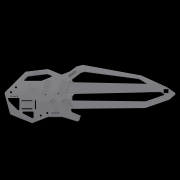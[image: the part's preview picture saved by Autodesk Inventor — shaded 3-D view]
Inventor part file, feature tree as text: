
AUTODESK INVENTOR PART (.ipt)
format: ipt  version: 2020 (Build 240168000, 168)  size: 9,547,776 bytes
history: native  units: in
note: dims shown in document units (in); Inventor stores cm internally (conversion verified against a paired STEP export)
features: other x165, extrude x70, fillet x51, projected_geometry x6, sketch x5, hole x4, loft x3, reference x2, plane x1, move_body x1
ambient origin geometry x8: Origin, YZ Plane, XZ Plane, XY Plane, X Axis, Y Axis, Z Axis, Center Point
bodies: Body (feature_tree), BodyFeature (feature_tree), BodyCut (feature_tree), BodyCutFeature (feature_tree), BodyCutFilletFeature (feature_tree), BodyCutCombineFeature (feature_tree), BodyCutEdgeFilletFeature (feature_tree), BodyRibFrontFilletsFeature (feature_tree), BodyBackRibFilletsFeature (feature_tree), BodyFretboardFilletsFeature (feature_tree), BodyFrontTopFilletsFeature (feature_tree), BodyFrontBottomFilletsFeature (feature_tree), BodyFrontNeckFilletsFeature (feature_tree), Solid22 (feature_tree), Solid23 (feature_tree), Solid62 (feature_tree), Solid64 (feature_tree), Solid65 (feature_tree), Solid68 (feature_tree), Solid50 (feature_tree), Solid52 (feature_tree), Solid54 (feature_tree), Solid56 (feature_tree), Solid57 (feature_tree), Solid59 (feature_tree)
feature tree (308):
  other  "MainBody"
  extrude  "NeckMountsProfileFeature"  Depth=0.5in TaperAngle=0.0deg
  other  "NeckPlane"
  extrude  "8StringFeature"  Depth=4.5in
  extrude  "6StringFeature"  Depth=1.12in
  extrude  "HornFeature"  Depth=0.6788in
  other  "6StringNeckFeature"
  other  "8StringNeckFeature"
  fillet  "InsideCornerFilletsFeature1/8"  Radius=0.6788in
  fillet  "OutsideFilletsFeature1/2"  Radius=0.125in
  fillet  "NeckMountOutsideFilletsFeature1/4"  Radius=0.5in
  fillet  "TipFilletsFeature1/8"  Radius=0.125in
  fillet  "BottomHornTipFilletFeature1/10"  Radius=0.1in
  fillet  "BottomHornFilletsFeature1/8"  Radius=0.125in
  fillet  "InsideHandleFilletsFeature1/2"  Radius=0.5in
  fillet  "InsideHandleFilletsFeature1/8"  Radius=0.125in
  fillet  "InsideTopHornFilletsFeature1/4"  Radius=0.25in
  fillet  "InsideTopHornFilletsFeature1/2"  Radius=0.5in
  fillet  "InsideBottomHornFilletsFeature1/4"  Radius=0.25in
  other  "PickupsOriginal"
  other  "MiddlePlane"
  other  "PickupsCustom"
  other  "PickupsModified"
  extrude  "TopPickupsIndentFeature"  Depth=0.05in
  extrude  "BottomPickupsIndentFeature"  Depth=0.05in
  extrude  "TopPickupHolesFeature"  Depth=0.05in
  extrude  "BottomPickupHolesFeature"  Depth=0.05in
  fillet  "PickupIndentFilletsFeature"  Radius=1.1649in
  other  "Frets"
  other  "FretsPreview"
  other  "TopHornHandleIndent"
  extrude  "TopHornBodyHandleFeature"  Depth=0.05in
  extrude  "TopHornHornHandleFeature"  Depth=0.05in
  other  "HornSculptFeature"
  other  "TopHornHandleFront"
  extrude  "TopHornHandleFrontFeature"  Depth=0.05in
  extrude  "TopHornHandleFront2Feature"  Depth=0.05in
  extrude  "TopHornHandleFront3Feature"  TaperAngle=45.0deg  [1 undecoded]
  other  "TopHornHandleBack"
  extrude  "TopHornHandleBackFeature"  TaperAngle=120.0deg  [1 undecoded]
  extrude  "TopHornHandleBack2Feature"  Depth=0.05in
  extrude  "TopHandleFeature"  Depth=0.05in
  extrude  "TopHandleFrontFeature"  Depth=0.05in
  extrude  "TopHandleBackFeature"  Depth=0.05in
  other  "Tuners"
  hole  "TunerHolesFeature"  [1 undecoded]
  other  "LogoMount"
  extrude  "LogoMountFeature"  Depth=0.05in
  other  "SideProfile"
  extrude  "SideProfileFeature"  Depth=0.05in
  other  "KeyboardCompartmentSidePlane"
  extrude  "KeyboardCompartmentFeature"  Depth=0.05in
  fillet  "KeyboardCompartmentFilletsFeature"  Radius=0.101in
  other  "ControlsBottom"
  other  "ControlsTop2"
  other  "ControlsTop1"
  extrude  "ControlsTop1Feature"  Depth=0.05in
  extrude  "ControlsTop2Feature"  Depth=0.05in
  extrude  "ControlsBottomFeature"  Depth=0.05in
  other  "HornSculptSideProfileFeature"
  fillet  "HornFretboardFilletFeature"  Radius=0.933in
  other  "ElectronicsCompartments"
  other  "InsideFacePlane1"
  other  "InsideFacePlane2"
  other  "InsideFacePlane3"
  extrude  "ElectronicCompartmentTopFeature"  Depth=0.05in
  extrude  "ElectronicCompartmentBottomFeature"  Depth=0.05in
  other  "ElectronicCompartmentsSculpt1Feature"
  other  "ElectronicCompartmentsSculpt2Feature"
  other  "ElectronicCompartmentsSculpt3Feature"
  other  "ElectronicCompartmentsSubtractFeature"
  extrude  "ElectronicCompartmentsSubtract2Feature"  Depth=0.05in
  fillet  "ElectronicCompartmentFillets1Feature"  Radius=3.5in
  fillet  "ElectronicCompartmentFillets2Feature"  Radius=1.277in
  extrude  "ControlIndentsBottomFeature"  Depth=0.05in
  fillet  "ElectronicCompartmentFillets3Feature"  Radius=1.5in
  fillet  "ElectronicCompartmentFillets4Feature"  Radius=1.0857in
  extrude  "ControlIndentsTopFeature"  Depth=0.05in
  other  "ControlIndents2Top"
  extrude  "ControlIndents2TopFeature"  Depth=0.05in
  fillet  "ControlIndents3FilletsFeature"  Radius=4.5in
  extrude  "ControlIndents2RecutFeature"  Depth=0.05in
  fillet  "ElectronicCompartmentInsideFilletsFeature"  Radius=0.1512in
  other  "BottomBridgePickupWirePlane"
  extrude  "BottomBridgePickupWireHoleFeature"  Depth=0.05in
  other  "BottomNeckPickupWirePlane"
  extrude  "BottomNeckPickupWireFeature"  Depth=0.05in
  extrude  "TopPickupWireFeature"  Depth=0.05in
  other  "SeaboardBlockCircuitboardMounts"
  extrude  "SeaboardBlockMountStemFeature"  Depth=0.05in
  extrude  "SeaboardBlockMountsFeature"  Depth=0.05in
  other  "SeaboardBlockKeyMounts"
  extrude  "SeaboardBlockKeyMountsFeature"  Depth=0.05in
  extrude  "SeaboardBlockRibbonsFeature"  Depth=0.05in
  extrude  "TunersTopFeature"  Depth=0.05in
  extrude  "TunersMiddleFeature"  Depth=0.05in
  extrude  "TunersBottomFeature"  Depth=0.05in
  fillet  "TunerFilletsFeature"  Radius=1.1386in
  extrude  "NeckCutFeature"  Depth=0.05in
  fillet  "NeckCutFilletFeature"  Radius=4.009in
  other  "NeckCutCombineFeature"
  fillet  "NeckCutEdgeFilletFeature"  Radius=1.481in
  fillet  "NeckCutCornerFilletsFeature"  Radius=0.25in
  extrude  "NeckMountsFeature"  Depth=0.05in
  extrude  "FretMarkersTopFeature"  Depth=0.05in
  extrude  "FretMarkersBottomFeature"  Depth=0.05in
  extrude  "FretsPreviewFeature"  TaperAngle=0.0deg  [1 undecoded]
  extrude  "FretLocksPreviewFeature"  Depth=0.3937in
  hole  "FretLocksHolesFeature"  [1 undecoded]
  extrude  "TopHornHandleBodyFeature"  Depth=0.05in
  other  "TopHornSculpt3Feature"
  other  "TopHornSculpt4Feature"
  other  "TopHornSculpt5Feature"
  fillet  "TopHornHandleBodyFilletsFeature"  Radius=0.9256in
  fillet  "TopHornHandleFilletsFeature"  [1 undecoded]
  other  "TopHornAdjustFeature"
  fillet  "TopHornAdjustFilletFeature"  [1 undecoded]
  other  "HandlePlane1"
  other  "HandlePlane2"
  other  "Handle"
  extrude  "HandleBackFeature"  Depth=0.05in
  extrude  "HandleFrontFeature"  Depth=0.05in
  other  "HandleSculpt1Feature"
  other  "HandleSculpt2Feature"
  other  "HandleSculpt3Feature"
  other  "HandleSculpt4Feature"
  other  "HandleSculpt5Feature"
  other  "HandleSculpt6Feature"
  other  "HandleEdit1Feature"
  other  "HandleEdit2Feature"
  fillet  "HandleBodyFilletsFeature"  Radius=25.5in
  fillet  "HandleRibFilletsFeature"  Radius=0.3333in
  other  "HornBackSculptFeature"
  other  "HornHandleBackSculpt1Feature"
  other  "HornHandleBackSculpt2Feature"
  fillet  "HornHandleackSculptFilletsFeature"  Radius=0.333in
  fillet  "HandleMeshFilletsFeature"  Radius=0.1in
  fillet  "HornMeshFillets1Feature"  Radius=0.1in
  fillet  "FretboardEndFilletsFeature"  [1 undecoded]
  other  "KeyboardCompartmentSideProfile"
  extrude  "KeyboardCompartmentExactFeature"  Depth=0.05in
  extrude  "KeyboardCompartmentSideFeature"  Depth=0.05in
  other  "KeyboardCompartmentExactSubtractFeature"
  other  "8NeckSplitFeature"
  other  "8NeckLoftStartPlane"
  other  "8NeckLoftEndPlane"
  loft  "8NeckLoftFeature"
  other  "6NeckSplitForLoftFeature"
  other  "6NeckLoftEndPlane"
  other  "6NeckLoftStartPlane"
  extrude  "OscScreenFeature"  TaperAngle=0.0deg  [1 undecoded]
  other  "OscCompartmentPlane"
  other  "OscIndentPlane"
  extrude  "OscCompartmentFeature"  Depth=0.05in
  other  "OscCompartmentSubtractFeature"
  extrude  "OscMountFeature"  Depth=0.05in
  other  "OscCoverIndentPlane"
  extrude  "OscCoverIndentFeature"  Depth=0.05in
  fillet  "OscCoverIndentFilletsFeature"  [1 undecoded]
  extrude  "OscCoverMountHolesFeature"  Depth=0.05in TaperAngle=0.0deg
  fillet  "ElectronicCompartmentLastFilletFeature"  Radius=0.3in
  loft  "6NeckLoftFeature"
  extrude  "6CloseCutFeature"  Depth=0.05in
  other  "HeadSculpt1Feature"
  other  "HeadThickness"
  other  "HeadSculpt2Feature"
  other  "HeadSculpt3Plane"
  extrude  "HeadSculpt3Feature"  Depth=0.05in
  other  "HeadSculpt4Feature"
  other  "8HeadCombineFeature"
  other  "8HeadCleanupFeature"
  fillet  "8HeadFilletFeature"  Radius=0.333in
  other  "HeadSculpt5Plane"
  other  "HeadSculpt5Feature"
  other  "HeadSculpt6Feature"
  other  "HeadSculpt7Plane"
  extrude  "HeadSculpt7Feature"  Depth=0.05in
  other  "6StringCombineFeature"
  other  "6NeckFilletSplitFeature"
  other  "8NeckFilletSplitFeature"
  fillet  "InsideHeadFilletFeature"  Radius=0.125in
  other  "CombineFilletsFeature"
  fillet  "HornHeadFilletsFeature"  Radius=0.5in
  fillet  "HornFillet3Feature"  Radius=5.55in
  other  "HornFinalSplitFeature"
  other  "6FinalSplitFeature"
  other  "6CombineFeature"
  other  "8NeckJoin"
  other  "6NeckJoin"
  extrude  "8NeckJoinFeature"  Depth=0.05in
  fillet  "8NeckJoinFilletFeature"  Radius=0.2in
  extrude  "6NeckJoinFeature"  Depth=0.05in
  extrude  "SeaboardBlockMountHolesFeature"  TaperAngle=0.0deg  [1 undecoded]
  extrude  "PickupRecutFeature"  Depth=0.05in
  extrude  "BackCoverIndentFeature"  Depth=0.3937in
  extrude  "ElectronicsCompartmentSupportFeature"  Depth=0.05in
  fillet  "ElectronicsCompartmentSupportFilletsFeature"  Radius=1.125in
  hole  "BackCoverMountsFeature"  [1 undecoded]
  other  "OscCoverBottom"
  other  "OscCoverTopPlane"
  other  "OscCoverMounts"
  loft  "OscCoverFeature"
  extrude  "OscCoverBodyCutFeature"  Depth=0.05in TaperAngle=0.0deg
  fillet  "OscCoverBodyCutFilletsFeature"  Radius=0.05in
  other  "OscCoverBodyCutSubtractFeature"
  fillet  "OscCoverBodyFilletFeature"  Radius=0.125in
  extrude  "OscCoverMountsFeature"  Depth=0.05in
  other  "LogoCompartment"
  extrude  "LogoCompartmentFeature"  Depth=0.05in
  extrude  "LogoCompartmentMountsFeature"  Depth=0.05in
  fillet  "LogoCompartmentFillet1Feature"  Radius=0.5in
  fillet  "LogoCompartmentFillet2Feature"  Radius=0.25in
  fillet  "LogoCompartmentFillet3Feature"  Radius=0.1in
  fillet  "LogoCompartmentFillet4Feature"  Radius=0.13in
  fillet  "LogoCompartmentFillet5Feature"  Radius=3.063in
  fillet  "LogoCompartmentFillet6Feature"  Radius=0.1295in
  fillet  "LogoCompartmentFillet7Feature"  Radius=0.1295in
  fillet  "LogoCompartmentFillet8Feature"  Radius=0.5708in
  hole  "LogoCompartmentHolesFeature"  [1 undecoded]
  other  "KeyboardCompartment"
  other  "TopHandle"
  other  "TunerLocksBody"
  other  "FretsBody"
  other  "TunersTop"
  other  "TunersMiddle"
  other  "TunersBottom"
  other  "ElectronicCompartments1Body"
  other  "NeckCut"
  other  "NeckMounts"
  other  "TopHornHandle"
  other  "TopHornHandleBody"
  projected_geometry  "Projected Loop22"
  projected_geometry  "Projected Loop23"
  other  "TopHandleFront"
  projected_geometry  "Projected Loop24"
  other  "TopHandleBack"
  other  "HandleBody"
  other  "TopHornSculpt3Plane"
  other  "TopHornSculpt4Plane"
  other  "TopHornSculpt5Plane"
  other  "HandleSculpt1Plane"
  other  "HandleSculpt2Plane"
  other  "HandleSculpt3Plane"
  other  "HandleSculpt4Plane"
  other  "HandleSculpt5Plane"
  other  "HandleSculpt6Plane"
  other  "HornBody"
  other  "8StringBody"
  other  "6StringBody"
  other  "NeckMountsProfile"
  other  "HornBackSculptPlane"
  other  "HornSculptFrontPlane"
  plane  "Work Plane62"
  other  "8NeckStartProfile"
  other  "8NeckEndProfile"
  sketch  "Sketch127"  dims[d8=0.7696in d18=0.5in d119=1.75in d120=0.0in]
  other  "6NeckLoftStartProfile"
  other  "6NeckLoftEndProfile"
  projected_geometry  "Projected Loop27"
  other  "6CloseCut"
  sketch  "Sketch131"  dims[d433=1.0857in d464=4.5in d466=0.25in]
  other  "HeadSculpt1Plane"
  other  "HeadSculpt2Plane"
  other  "HeadSculpt3Profile"
  other  "HeadSculpt4Plane"
  other  "HeadSculpt7Profile"
  other  "6NeckFilletSplit"
  other  "8NeckFilletSplit"
  sketch  "Sketch138"  dims[d501=0.25in d582=1.12in]
  sketch  "Sketch139"  dims[d644=25.0in d654=0.6788in d681=0.6788in d700=0.125in d702=0.5in d703=0.125in d705=0.1in d706=0.125in d707=0.5in d708=0.125in d709=0.25in d710=0.5in d711=0.25in]
  other  "ControlIndentsBottom"
  other  "BottomBridgePickupWireHole"
  other  "BottomNeckPickupWire"
  other  "TopPickupWire"
  other  "HornHandleBackSculpt1Plane"
  other  "HornHandleBackSculpt2Plane"
  sketch  "Sketch165"  dims[d716=2.2835in d717=0.0515in d718=13.825in d719=0.213in d721=0.9414in d722=1.1649in d724=5.7in d725=7.5379in d726=0.2542in d727=2.0in d728=45.0deg d729=120.0deg d730=0.3642in d731=0.9371in d745=5.6289in d747=6.0in d748=4.3in d750=0.8658in d751=0.6506in d753=0.4054in d754=0.8in d779=0.101in d781=1.7in d782=7.125in d783=2.6in d784=0.933in d787=1.1in d792=3.625in d793=4.0in d819=3.5in d825=1.277in d834=1.277in d836=1.5in d837=1.0857in d838=3.0in d839=2.0in d841=4.5in d846=3.3665in d850=0.1512in d853=2.6in d864=1.5757in d961=0.5in d962=0.5in d963=0.3779in d964=0.3779in d965=0.45in d966=0.45in d967=0.8795in d968=1.1386in d969=1.1386in d970=0.45in d971=4.009in d972=1.481in d979=0.25in d980=0.25in d982=0.1718in d983=0.1718in d984=0.0in d985=0.7874in d987=4.0in d988=0.3937in d990=1.0in d994=2.746in d995=1.481in d996=0.9256in d999=0.0in d1000=0.0in d1022=26.75in d1023=28.0in d1024=25.5in d1026=0.3333in d1041=0.333in d1042=0.1in d1044=0.1in d1048=0.0in d1049=0.0in d1054=0.1in d1055=0.1in d1057=0.748in d1060=0.0in d1061=0.0in d1064=0.4662in d1092=0.7in d1095=1.7in d1100=0.0in d1101=0.0in d1117=0.25in d1118=0.0in d1119=0.3in d1120=0.0in d1122=0.2in d1123=0.0in d1277=0.6459in d1329=0.5333in d1334=0.333in d1335=0.5333in d1339=0.125in d1348=0.5in d1358=5.55in d1359=1.75in d1373=0.2in d1375=0.1in d1376=0.0in d1406=1.125in d1430=3.1496in d1432=0.525in d1433=0.3937in d1435=1.0in d1439=1.8in d1440=1.125in d1441=0.2in d1475=0.1in d1476=0.75in d1477=0.375in d1478=0.25in d1479=0.5635in d1480=0.5in d1481=0.8108in d1483=0.05in d1484=0.0in d1485=0.05in d1486=0.0in d1487=0.05in d1488=0.0in d1489=0.125in d1490=0.1in d1491=2.846in d1492=1.481in d1493=0.5in d1494=0.25in d1496=0.1in d1504=0.13in d1508=0.1in d1511=3.063in d1512=0.1295in d1513=0.1295in d1526=0.5708in d1527=0.1286in d1528=1.3799in d1529=1.3958in d1530=1.1055in d1531=0.8208in d1534=2.3622in d1536=0.45in d1537=0.3937in d1539=1.0in d1574=1.0in d1575=0.0in d1576=0.0in d1577=0.4789in d1578=0.4308in d1579=1.1471in d1580=2.5in d1581=1.275in d1582=1.1845in d1583=1.481in d1584=1.1384in d1585=0.7644in d1586=2.746in d1587=0.264in d1588=0.4in d1589=0.0in d1590=0.75in d1591=0.0in d1592=1.0in d1593=0.0in d1594=1.0in d1595=0.0in d1596=0.144in d1597=3.75in d1598=0.1295in d1599=0.1295in d1638=10.0in d1639=14.2465in d1641=11.25in d1648=0.5in d1649=0.0in d1650=28.0in d1657=1.0in d1659=5.5in d1660=4.25in d1662=0.3333in d1663=0.0in d1664=10.0in d1665=1.0in d1671=0.1in d1672=0.5in d1676=3.0in d1677=2.425in d1682=0.75in d1683=0.0in d1690=1.1878in d1691=0.9817in d1692=1.0844in d1693=0.8784in d1695=0.2in d1696=0.0in d1750=1.525in d1751=0.0in d1752=0.5in d1777=0.5in d1778=0.0in d1779=0.5in d1780=0.0in d1781=0.5in d1782=0.0in d1783=0.6in d1784=0.0in d1790=0.65in d1791=0.0in d1792=0.65in d1793=0.0in d1795=0.125in d1821=0.1in d1828=0.0in d1829=0.0in d1830=0.475in d1831=0.125in d1832=0.125in d1843=3.0403in d1844=2.1333in d1845=0.758in d1847=1.75in d1848=0.0in d1849=1.9in d1850=0.0in d1851=1.9in d1852=0.0in d1858=0.9in d1859=0.0in d1862=0.0in d1863=0.0in d1864=0.5in d1865=0.0in d1866=0.5in d1867=0.0in d1870=0.2056in d1871=0.257in d1872=0.0674in d1875=0.25in d1876=0.0in d1877=0.15in d1880=0.15in d1882=0.05in d1883=0.05in d1885=1.3537in d1887=10.0in d1888=0.1in d1889=0.1in d1890=20.0in d1891=20.0in d1894=0.0618in d1900=0.1in d1901=0.4524in d1903=0.006in d1904=0.0in d1915=0.22in d1921=0.0in d1922=90.0deg d1923=0.0in d1924=90.0deg d1925=1.2in d1926=0.7in d1927=0.3333in d1928=0.001in d1929=0.25in d1930=1.25in d1931=0.25in d1935=0.8in d1936=0.3489in d1937=0.22in d1938=0.25in d1939=0.5in d1940=0.6in d1941=0.15in d1942=0.4in d1943=0.0in d1944=90.0deg d1945=0.0in d1946=90.0deg d1948=1.3333in d1949=2.125in d1951=1.125in d1952=2.55in d1957=3.0in d1958=0.1in d1959=0.1in d1960=0.1in d1961=1.0in d1962=0.0in d1966=1.0in d1967=0.0in d1968=0.44in d1969=0.0in d1975=0.1in d1976=0.1in d1980=10.6875in d1981=5.1875in d1982=0.85in d1983=0.3333in d1985=7.5816in d1987=0.1in d1988=0.0in d1989=0.1875in d1990=0.5333in d1992=150.0deg d1993=3.25in d1996=-0.325in d1997=-0.125in d1998=1.0in d1999=0.0in d2004=0.5in d2005=0.0in d2007=0.0938in d2008=0.5in d2009=0.25in d2010=2.3125in d2011=0.7188in d2015=0.25in d2016=5.0in d2019=0.125in d2020=0.25in d2027=0.2in d2028=0.0in d2029=0.02in d2030=0.0in d2039=0.55in d2047=0.25in d2048=0.25in d2049=0.0in d2050=0.0in d2052=2.295in d2053=0.0in d2056=0.25in d2058=0.25in d2059=0.3333in d2060=0.3333in d2061=0.25in d2062=0.3333in d2063=0.3333in d2064=0.0in d2065=0.0in d2066=0.339in d2067=0.1643in d2068=0.1in d2069=0.1in d2070=0.1in d2071=0.1in d2072=0.1643in d2073=0.1643in d2074=0.1643in d2077=3.3125in d2078=3.313in d2079=0.305in d2080=0.3333in d2081=1.0in d2082=0.0in d2083=0.3333in d2084=0.0in d2086=0.719in d2087=2.3125in d2088=0.125in d2089=0.1in d2090=0.438in d2091=0.438in d2092=0.438in d2093=0.438in d2094=0.25in d2095=0.0in d2096=0.25in d2097=0.25in d2098=2.0in d2100=2.5in d2102=0.75in d2103=0.25in d2104=0.25in d2105=0.0in d2106=0.625in d2111=10.0in d2112=0.125in d2113=0.3333in d2117=1.75in d2118=1.25in d2119=1.625in d2120=0.25in d2121=1.0in d2122=0.1in d2125=0.7in d2132=1.625in d2133=1.0in d2134=0.1in d2135=1.0in d2136=1.0in d2137=0.1in d2138=1.025in d2139=1.025in d2140=0.5in d2141=0.7in d2142=1.075in d2143=0.7in d2144=0.5in d2146=0.25in d2147=0.25in d2148=0.5in d2149=1.75in d2150=0.0in d2151=0.0in d2152=0.035in d2153=0.0in d2154=0.0in d2155=0.0in d2156=-0.325in d2157=1.0in d2158=0.2in d2159=0.0in d2160=1.0in d2161=0.2in d2162=0.0in d2164=1.0in d2165=2.2612in d2166=0.605in d2167=0.01in d2168=0.3333in d2169=0.5388in d2170=0.4in d2171=2.625in d2172=1.375in d2173=0.172in d2174=0.281in d2175=0.5in d2176=0.0in d2177=-2.0in d2178=1.797in d2179=0.0in d2180=-0.125in d2181=0.06in d2182=0.06in d2183=0.505in d2184=0.9375in d2185=2.625in d2186=1.375in d2187=2.5in d2188=1.0313in d2189=0.05in d2190=0.1719in d2191=0.0625in d2192=0.0625in d2193=0.1094in d2194=0.0312in d2195=0.0312in d2196=0.0312in d2197=0.0312in d2198=0.0312in d2199=0.0312in d2200=0.0312in d2201=0.0312in d2202=0.203in d2203=0.0in d2207=-0.2in d2211=0.15in d2212=1.0in d2213=0.0in d2214=0.15in d2215=0.15in d2216=0.1in d2220=0.05in d2221=1.5in d2222=0.0in d2230=0.6836in d2238=1.0in d2239=0.25in d2240=0.1in d2241=0.0689in d2243=1.1408in d2244=0.449in d2245=1.6223in d2246=2.1038in d2247=0.449in d2248=0.0463in d2249=0.4549in d2251=0.3908in d2252=0.3908in d2255=0.8in d2257=3.5in d2259=1.1973in d2261=0.625in d2262=0.625in d2263=0.536in d2264=2.7in d2265=0.25in d2266=0.2in d2267=0.0in d2268=0.2in d2269=0.0in d2278=0.4264in d2279=1.0in d2280=0.0in d2281=21.986in d2282=0.0in d2283=0.1in d2284=0.1in d2285=0.5in d2286=0.0in d2287=0.5333in d2288=0.1in d2293=0.85in d2294=1.0in d2295=0.25in d2296=0.749in d2297=0.0in d2298=0.25in d2299=0.1984in d2300=0.1in d2301=0.0in d2302=0.2in d2303=0.0in d2304=0.481in d2305=0.481in d2306=0.5in d2307=0.25in d2308=0.1in d2309=0.75in d2310=0.375in d2311=0.25in d2312=0.5635in d2313=0.5in d2314=0.8108in d2319=0.0in d2320=0.0in d2321=90.0deg d2322=0.0in d2323=90.0deg d2324=0.5in d2325=0.0in d2326=28.0in d2327=1.0in d2328=1.5in d2329=0.0in d2330=0.2in d2331=0.2in d2333=0.22in d2335=0.12in d2336=0.12in d2337=0.1in d2338=0.1in d2339=0.75in d2340=0.375in d2341=0.25in d2342=0.5635in d2343=0.5in d2344=0.8108in d2347=0.25in d2348=0.3in d2349=0.15in d2350=0.15in d2351=0.3in d2352=0.15in d2353=0.3in d2354=0.25in d2355=0.25in d2356=0.25in d2357=0.25in d2358=0.25in d2359=0.1958in d2360=0.1958in d2365=0.2in d2366=0.0in d2381=0.7in d2382=0.6in d2387=0.089in d2408=0.3333in d2409=0.0in d2410=0.031in d2412=0.106in d2413=0.072in d2414=0.033in d2415=0.125in d2416=0.132in d2417=0.101in d2418=0.074in d2419=0.05in d2420=0.75in d2421=0.375in d2422=0.25in d2423=0.5635in d2424=0.5in d2425=0.8108in d620=0.5in d621=0.0344in d622=0.5in d623=0.0344in d1625=0.5in d1626=0.0344in d1627=0.5in d1628=0.0344in d1730=0.5in d1731=0.0344in d1732=0.5in d1733=0.0344in d1822=0.5in d1823=0.0344in d1824=0.5in d1825=0.0344in d1837=0.5in d1838=0.0344in d1839=0.5in d1840=0.0344in d1860=0.5in d1861=0.0344in d1947=0.5in d1950=0.0344in d2012=0.5in d2013=0.0344in d2101=0.5in d2392=0.5in d2393=0.0344in d2394=0.5in d2395=0.0344in]
  other  "OscScreen"
  other  "OscCompartment"
  other  "OscMount"
  other  "OscCoverPlane"
  other  "OscCoverIndent"
  other  "OscCoverMountHoles"
  projected_geometry  "Projected Loop32"
  other  "KeyboardCompartmentExact"
  projected_geometry  "Projected Loop35"
  other  "SeaboardBlockMountHoles"
  reference  "Reference6"
  reference  "Reference7"
  other  "PickupRecut"
  other  "BackCoverIndent"
  other  "ElectronicsCompartmentSupport"
  other  "BackCoverMounts"
  other  "OscCoverTop"
  other  "OscCoverBody"
  other  "Delete13"
  move_body  "Move3"
  other  "Delete14"
  other  "6StringNeckCombineBody"
  other  "8StringNeckBody"
  other  "6StringNeckBody"
  other  "TopHornBody"
  other  "8StringCombinedBody"
  other  "6StringCombinedBody"
  other  "Delete18"
  other  "<userpath>\Desktop\switchback\src\switchback-exploded.iam"
  other  "switchback-exploded.iam"
  other  "seaboard-block-keyboard:1"
note: 13 required parameter values undecoded (feature->parameter linkage not recoverable at this tier; creation-order binding heuristic only, values carry confidence <= 0.55)
